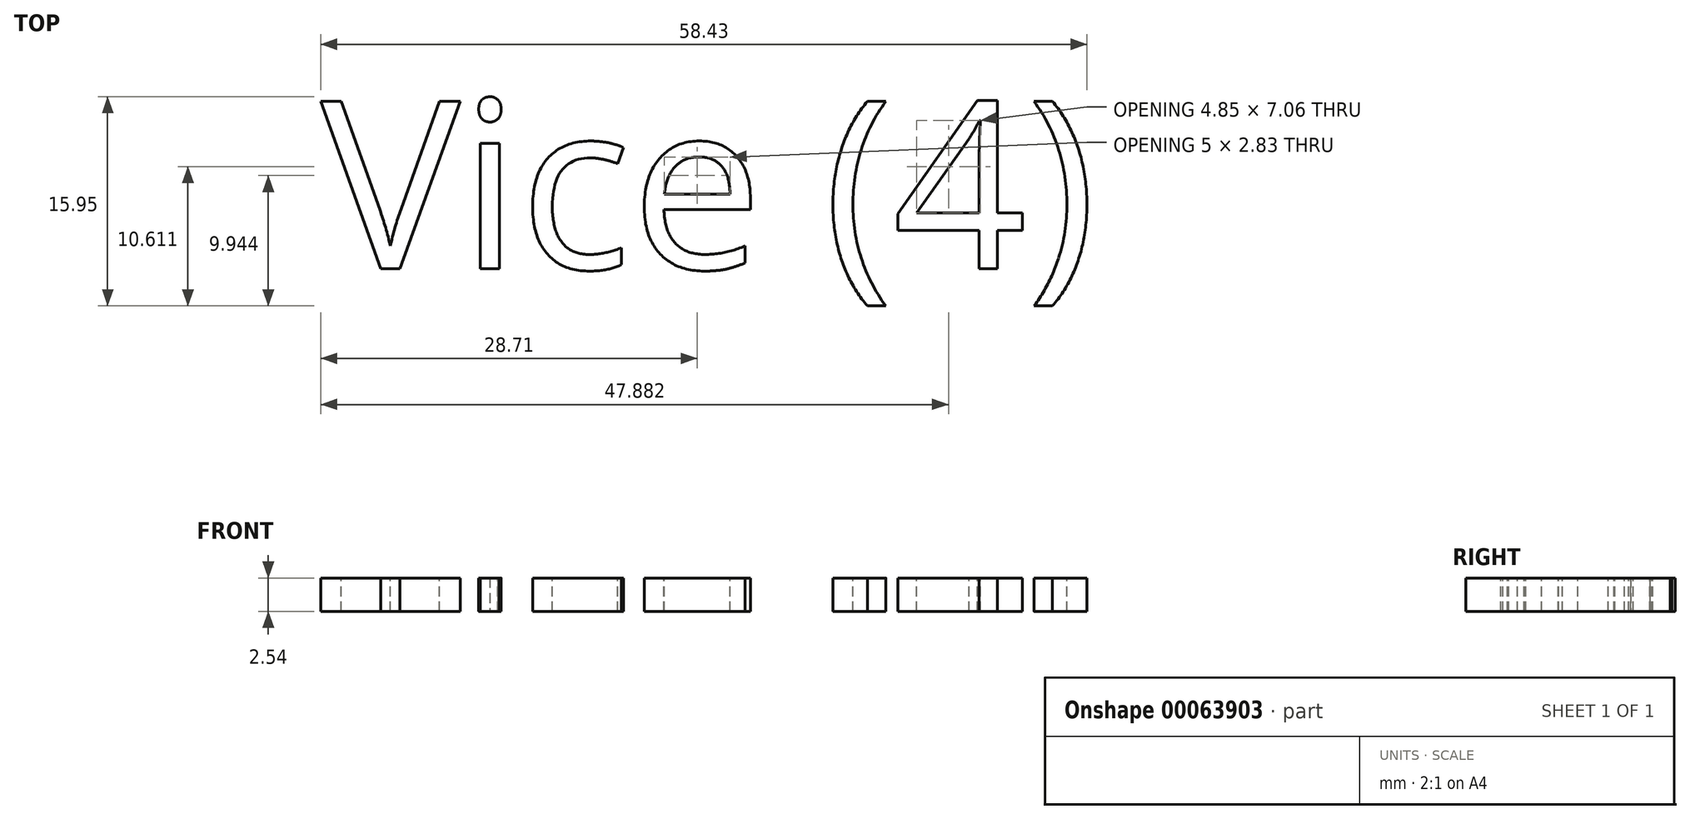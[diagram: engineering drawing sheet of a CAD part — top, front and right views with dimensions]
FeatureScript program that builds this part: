
annotation { "Feature Type Name" : "Feature", "Feature Type Description" : "" }
export const myFeature = defineFeature(function(context is Context, id is Id, definition is map)
    precondition{}
    {
        {
            var Q0;
            Q0=qCreatedBy(makeId("Top.planeOp"),FACE);
            var sketch = newSketch(context, id + "F0", { "sketchPlane" : qUnion([Q0])});
            skLineSegment(sketch, "E0.bottom", {"start": v(0, 0) * mm, "end": v(127, 0) * mm});
            skLineSegment(sketch, "E0.top", {"start": v(0, 127) * mm, "end": v(127, 127) * mm});
            skLineSegment(sketch, "E0.left", {"start": v(0, 0) * mm, "end": v(0, 127) * mm});
            skLineSegment(sketch, "E0.right", {"start": v(127, 0) * mm, "end": v(127, 127) * mm});
            skSolve(sketch);
        }
        {
            var Q0;
            Q0 = qSketchRegion(id + "F0", true);
            extrude(context, id + "F1", {"entities" : qUnion([Q0]), "depth" : 2.54 * mm});
        }
        {
            var Q0;
            Q0=makeQuery(id+"F1.opExtrude","CAP_FACE",FACE,{"disambiguationData":[OSD([sQuery(id+"F0.wireOp",EDGE,"E0.bottom"),sQuery(id+"F0.wireOp",EDGE,"E0.top"),sQuery(id+"F0.wireOp",EDGE,"E0.left"),sQuery(id+"F0.wireOp",EDGE,"E0.right")])],"isStart":false});
            var sketch = newSketch(context, id + "F2", { "sketchPlane" : qUnion([Q0])});
            skText(sketch, "E1", { "text": "Vice (4)", "fontName": "OpenSans-Regular.ttf"});
            const initialGuessF2  = {"E1": [0.05163, 0.04437, 1, 0, 0.01287]};
            skSetInitialGuess(sketch, initialGuessF2);
            skSolve(sketch);
        }
        {
            var Q0;
            Q0=makeQuery(id+"F2.imprint","IMPRINT",FACE,{"disambiguationData":[TD([[makeQuery(id+"F2.imprint","IMPRINT",EDGE,{"derivedFrom":sQuery(id+"F2.wireOp",EDGE,"E1.sketch_text.stroke-50")}),1.0]])]});
            var Q1;
            Q1=makeQuery(id+"F2.imprint","IMPRINT",FACE,{"disambiguationData":[TD([[makeQuery(id+"F2.imprint","IMPRINT",EDGE,{"derivedFrom":sQuery(id+"F2.wireOp",EDGE,"E1.sketch_text.stroke-76")}),1.0]])]});
            var Q2;
            Q2=makeQuery(id+"F2.imprint","IMPRINT",FACE,{"disambiguationData":[TD([[makeQuery(id+"F2.imprint","IMPRINT",EDGE,{"derivedFrom":sQuery(id+"F2.wireOp",EDGE,"E1.sketch_text.stroke-0")}),1.0]])]});
            extrude(context, id + "F3", {"entities" : qUnion([Q0, Q1, Q2]), "operationType" : NewBodyOperationType.REMOVE, "oppositeDirection" : true, "depth" : 25.4 * mm});
        }
    });
